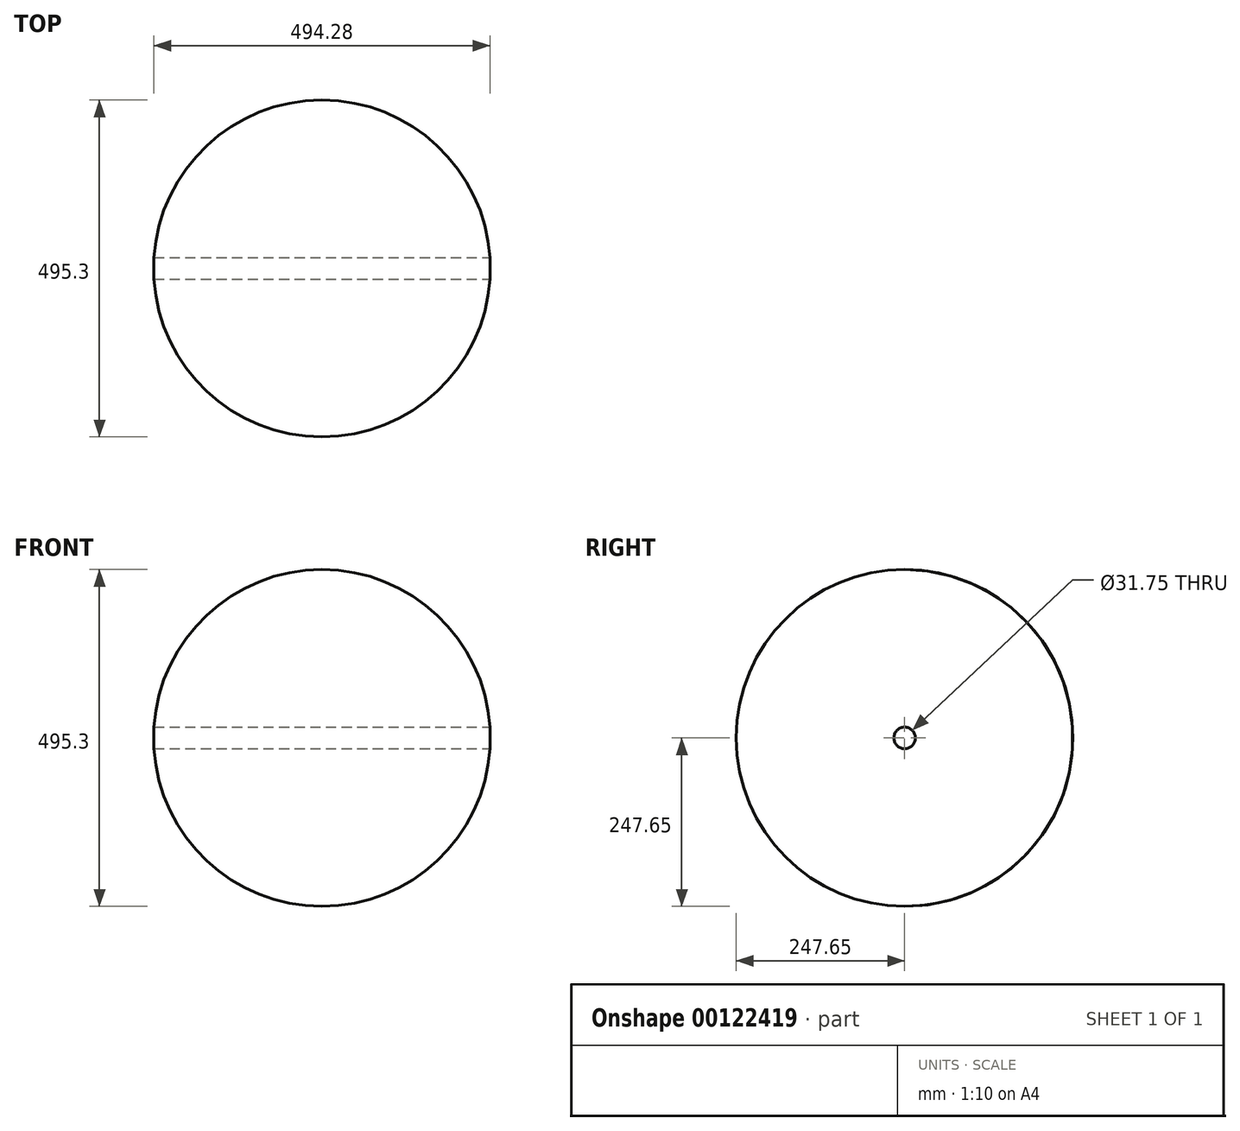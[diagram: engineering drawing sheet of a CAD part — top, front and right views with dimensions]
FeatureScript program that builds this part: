
annotation { "Feature Type Name" : "Feature", "Feature Type Description" : "" }
export const myFeature = defineFeature(function(context is Context, id is Id, definition is map)
    precondition{}
    {
        {
            var Q0;
            Q0=qCreatedBy(makeId("Front.planeOp"),FACE);
            var sketch = newSketch(context, id + "F0", { "sketchPlane" : qUnion([Q0])});
            skCircle(sketch, "E0", {"center": v(0, 0) * mm, "radius": 247.65 * mm});
            skLineSegment(sketch, "E1", {"start": v(0, 0) * mm, "end": v(0, 247.65) * mm});
            skLineSegment(sketch, "E2", {"start": v(0, 247.65) * mm, "end": v(0, -247.65) * mm});
            skLineSegment(sketch, "E3", {"start": v(0, -247.65) * mm, "end": v(0, 247.65) * mm});
            skSolve(sketch);
        }
        {
            var Q0;
            {var subQ0=sQuery(id+"F0.wireOp",EDGE,"E1");Q0=makeQuery(id+"F0.imprint","IMPRINT",FACE,{"disambiguationData":[TD([[makeQuery(id+"F0.imprint","IMPRINT",EDGE,{"derivedFrom":subQ0}),1.0]])]});}
            var Q1;
            Q1=sQuery(id+"F0.wireOp",EDGE,"E3");
            revolve(context, id + "F1", {"entities" : qUnion([Q0]), "axis" : qUnion([Q1]), "revolveType" : RevolveType.FULL});
        }
        {
            var Q0;
            Q0=qCreatedBy(makeId("Right.planeOp"),FACE);
            var sketch = newSketch(context, id + "F2", { "sketchPlane" : qUnion([Q0])});
            skCircle(sketch, "E4", {"center": v(0, 0) * mm, "radius": 15.88 * mm});
            skSolve(sketch);
        }
        {
            var Q0;
            Q0 = qSketchRegion(id + "F2", true);
            extrude(context, id + "F3", {"entities" : qUnion([Q0]), "operationType" : NewBodyOperationType.REMOVE, "endBound" : BoundingType.SYMMETRIC, "oppositeDirection" : true, "depth" : 558.8 * mm, "offsetDistance" : 25.4 * mm});
        }
    });
